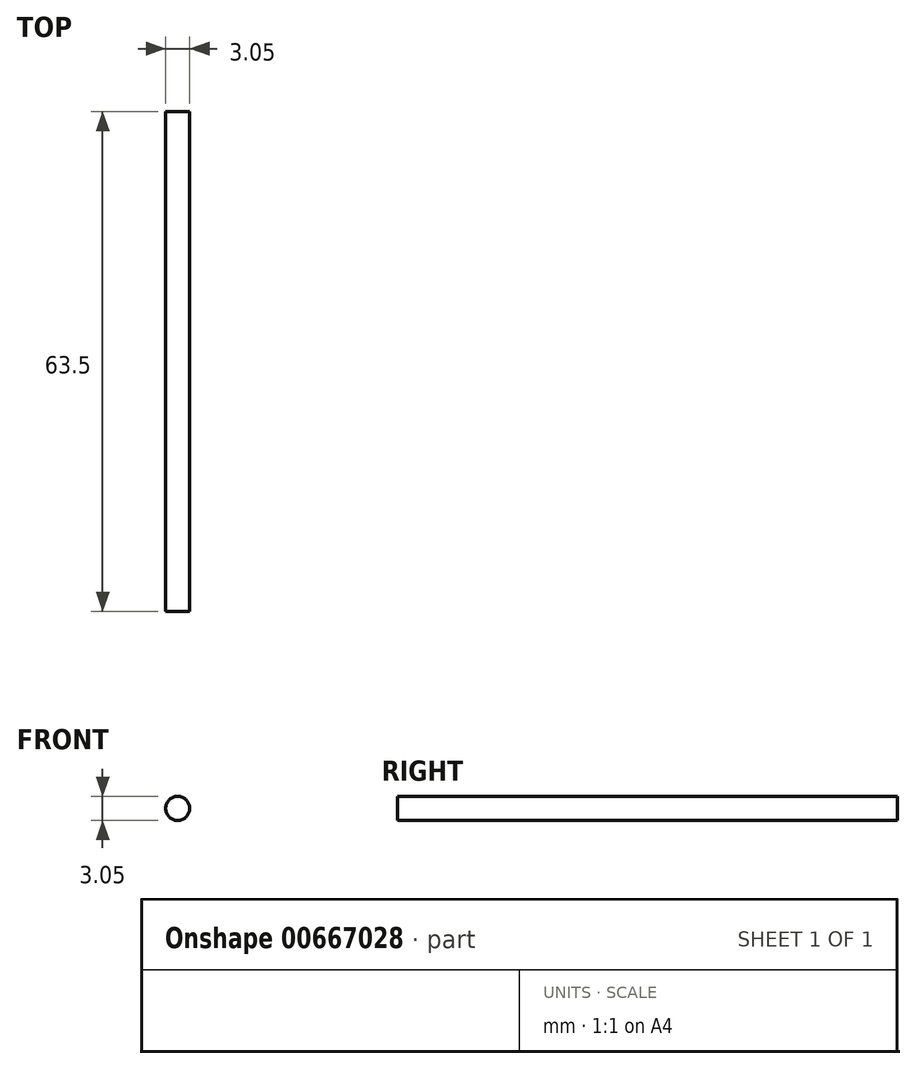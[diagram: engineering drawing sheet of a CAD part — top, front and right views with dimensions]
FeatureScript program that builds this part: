
annotation { "Feature Type Name" : "Feature", "Feature Type Description" : "" }
export const myFeature = defineFeature(function(context is Context, id is Id, definition is map)
    precondition{}
    {
        {
            var Q0;
            Q0=qCreatedBy(makeId("Front.planeOp"),FACE);
            var sketch = newSketch(context, id + "F0", { "sketchPlane" : qUnion([Q0])});
            skCircle(sketch, "E0", {"center": v(-20.96, 27.3) * mm, "radius": 1.52 * mm});
            skSolve(sketch);
        }
        {
            var Q0;
            Q0 = qSketchRegion(id + "F0", true);
            extrude(context, id + "F1", {"entities" : qUnion([Q0]), "depth" : 63.5 * mm, "offsetDistance" : 25.4 * mm});
        }
    });
